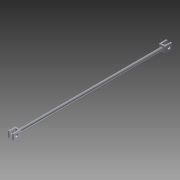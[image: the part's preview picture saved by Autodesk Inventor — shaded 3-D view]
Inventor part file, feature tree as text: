
AUTODESK INVENTOR PART (.ipt)
format: ipt  version: 2012 (Build 160160000, 160)  size: 133,632 bytes
history: native  units: in
note: dims shown in document units (in); Inventor stores cm internally (conversion verified against a paired STEP export)
features: extrude x3, sketch x3, projected_geometry x2, fillet x1
ambient origin geometry x8: Origin, YZ Plane, XZ Plane, XY Plane, X Axis, Y Axis, Z Axis, Center Point
bodies: Solid1 (feature_tree)
feature tree (9):
  extrude  "Extrusion1"  Depth=0.5in
  extrude  "Extrusion2"  Depth=0.625in
  extrude  "Extrusion3"  Depth=0.625in
  fillet  "Fillet1"  Radius=0.5in
  sketch  "Sketch1"  dims[d0=0.5in d1=0.5in]
  sketch  "Sketch2"  dims[d2=13.5in d3=0.0in d4=0.625in]
  sketch  "Sketch3"  dims[d5=0.25in d6=0.625in d7=0.5in d8=0.5in d9=25.0in d10=0.0in d11=0.25in d12=0.25in d13=0.25in d14=0.25in d15=0.125in d16=0.25in d17=0.25in d18=0.25in d19=25.0in d20=0.0in d21=0.125in]
  projected_geometry  "Projected Loop1"
  projected_geometry  "Projected Loop2"
